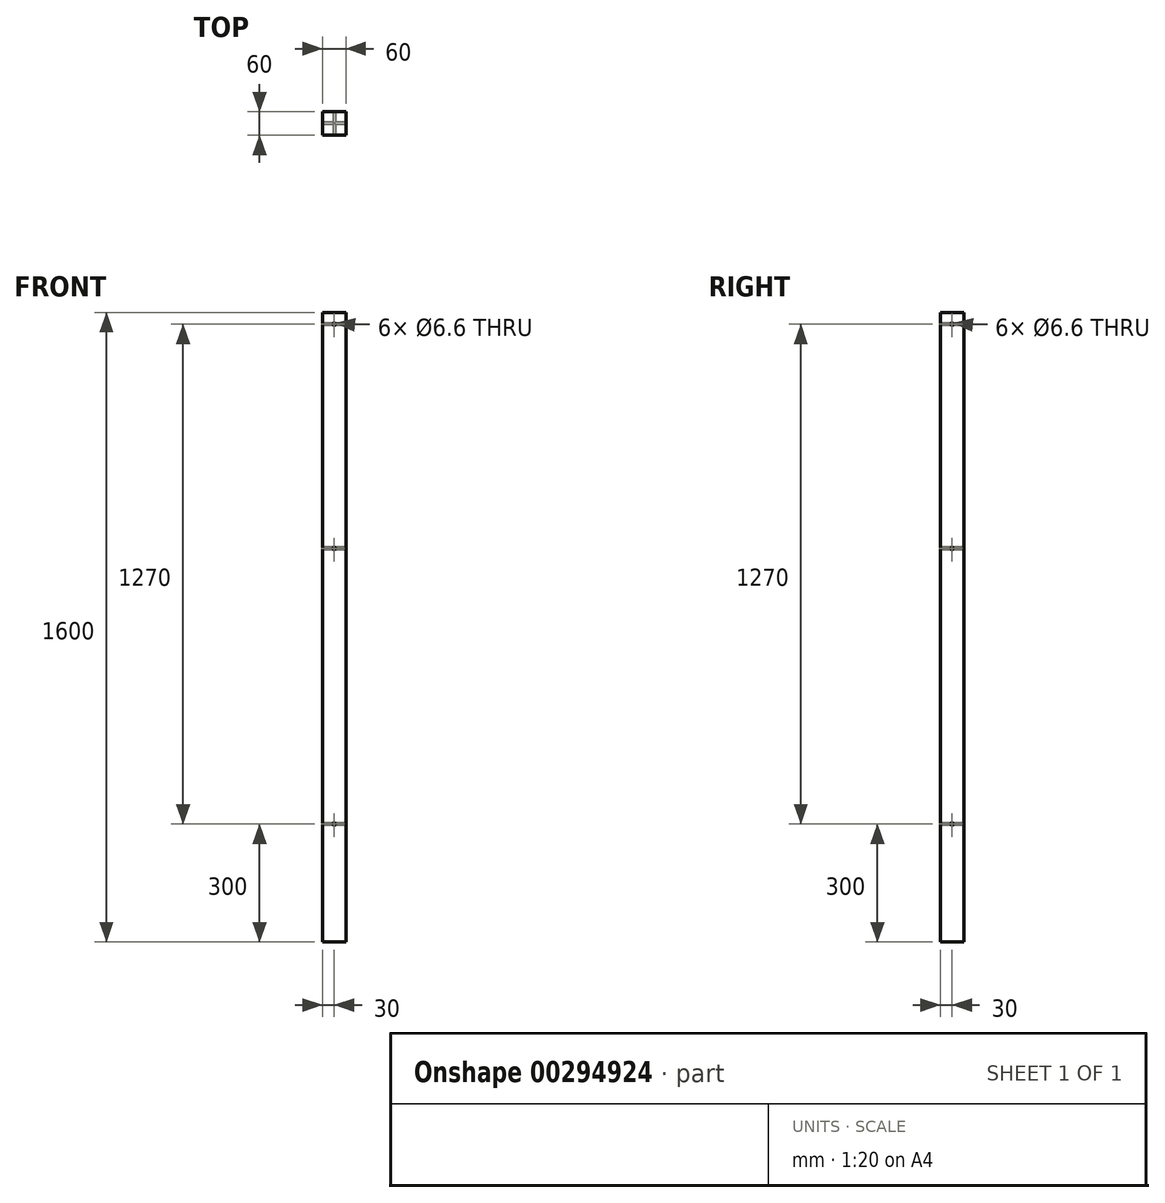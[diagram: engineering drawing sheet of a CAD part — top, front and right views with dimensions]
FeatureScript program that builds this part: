
annotation { "Feature Type Name" : "Feature", "Feature Type Description" : "" }
export const myFeature = defineFeature(function(context is Context, id is Id, definition is map)
    precondition{}
    {
        {
            var Q0;
            Q0=qCreatedBy(makeId("Top.planeOp"),FACE);
            var sketch = newSketch(context, id + "F0", { "sketchPlane" : qUnion([Q0])});
            skLineSegment(sketch, "E0.bottom", {"start": v(30, 30) * mm, "end": v(-30, 30) * mm});
            skLineSegment(sketch, "E0.top", {"start": v(30, -30) * mm, "end": v(-30, -30) * mm});
            skLineSegment(sketch, "E0.left", {"start": v(30, 30) * mm, "end": v(30, -30) * mm});
            skLineSegment(sketch, "E0.right", {"start": v(-30, 30) * mm, "end": v(-30, -30) * mm});
            skPoint(sketch, "E0.middle", {"position": v(0, 0) * mm});
            skSolve(sketch);
        }
        {
            var Q0;
            Q0=makeQuery(id+"F0.imprint","IMPRINT",FACE,{"disambiguationData":[TD([[makeQuery(id+"F0.imprint","IMPRINT",EDGE,{"derivedFrom":sQuery(id+"F0.wireOp",EDGE,"E0.bottom")}),1.0]])]});
            extrude(context, id + "F1", {"entities" : qUnion([Q0]), "depth" : 1600 * mm, "offsetDistance" : 25 * mm});
        }
        {
            var Q0;
            Q0=makeQuery(id+"F1.opExtrude","SWEPT_FACE",FACE,{"disambiguationData":[OSD([sQuery(id+"F0.wireOp",EDGE,"E0.right")])]});
            var sketch = newSketch(context, id + "F2", { "sketchPlane" : qUnion([Q0])});
            skPoint(sketch, "E1", {"position": v(0, 1570) * mm});
            skPoint(sketch, "E1.positionSnap0", {"position": v(0, 1600) * mm});
            skPoint(sketch, "E2", {"position": v(0, 300) * mm});
            skPoint(sketch, "E3", {"position": v(0, 1000) * mm});
            skSolve(sketch);
        }
        {
            var Q0;
            Q0=sQuery(id+"F2.wireOp",VERTEX,"E1");
            var Q1;
            Q1=sQuery(id+"F2.wireOp",VERTEX,"E2");
            var Q2;
            Q2=sQuery(id+"F2.wireOp",VERTEX,"E3");
            var Q3;
            Q3=makeQuery(id+"F1.opExtrude","SWEPT_BODY",BODY,{"disambiguationData":[OSD([sQuery(id+"F0.wireOp",EDGE,"E0.bottom"),sQuery(id+"F0.wireOp",EDGE,"E0.top"),sQuery(id+"F0.wireOp",EDGE,"E0.left"),sQuery(id+"F0.wireOp",EDGE,"E0.right")])]});
            hole(context, id + "F3", {"style" : HoleStyle.SIMPLE, "endStyle" : HoleEndStyle.THROUGH, "standardTappedOrClearance" : lookupTablePath({ "standard" : "ISO", "fit" : "Normal", "size" : "M6", "type" : "Clearance" }), "standardBlindInLast" : lookupTablePath({ "fit" : "Standard", "standard" : "ISO", "size" : "M6", "type" : "Clearance" }), "holeDiameter" : 6.6 * mm, "isTappedThrough" : true, "tappedDepth" : 12 * mm, "tapClearance" : 3, "locations" : qUnion([Q0, Q1, Q2]), "scope" : qUnion([Q3])});
        }
        {
            var Q0;
            Q0=makeQuery(id+"F1.opExtrude","SWEPT_FACE",FACE,{"disambiguationData":[OSD([sQuery(id+"F0.wireOp",EDGE,"E0.top")])]});
            var sketch = newSketch(context, id + "F4", { "sketchPlane" : qUnion([Q0])});
            skPoint(sketch, "E4", {"position": v(0, 1570) * mm});
            skPoint(sketch, "E4.positionSnap0", {"position": v(0, 1600) * mm});
            skPoint(sketch, "E5", {"position": v(0, 300) * mm});
            skPoint(sketch, "E6", {"position": v(0, 1000) * mm});
            skSolve(sketch);
        }
        {
            var Q0;
            Q0=sQuery(id+"F4.wireOp",VERTEX,"E4");
            var Q1;
            Q1=sQuery(id+"F4.wireOp",VERTEX,"E5");
            var Q2;
            Q2=sQuery(id+"F4.wireOp",VERTEX,"E6");
            var Q3;
            Q3=makeQuery(id+"F1.opExtrude","SWEPT_BODY",BODY,{"disambiguationData":[OSD([sQuery(id+"F0.wireOp",EDGE,"E0.bottom"),sQuery(id+"F0.wireOp",EDGE,"E0.top"),sQuery(id+"F0.wireOp",EDGE,"E0.left"),sQuery(id+"F0.wireOp",EDGE,"E0.right")])]});
            hole(context, id + "F5", {"style" : HoleStyle.SIMPLE, "endStyle" : HoleEndStyle.THROUGH, "standardTappedOrClearance" : lookupTablePath({ "standard" : "ISO", "fit" : "Normal", "size" : "M6", "type" : "Clearance" }), "standardBlindInLast" : lookupTablePath({ "fit" : "Standard", "standard" : "ISO", "size" : "M6", "type" : "Clearance" }), "holeDiameter" : 6.6 * mm, "isTappedThrough" : true, "tappedDepth" : 12 * mm, "tapClearance" : 3, "locations" : qUnion([Q0, Q1, Q2]), "scope" : qUnion([Q3])});
        }
    });
